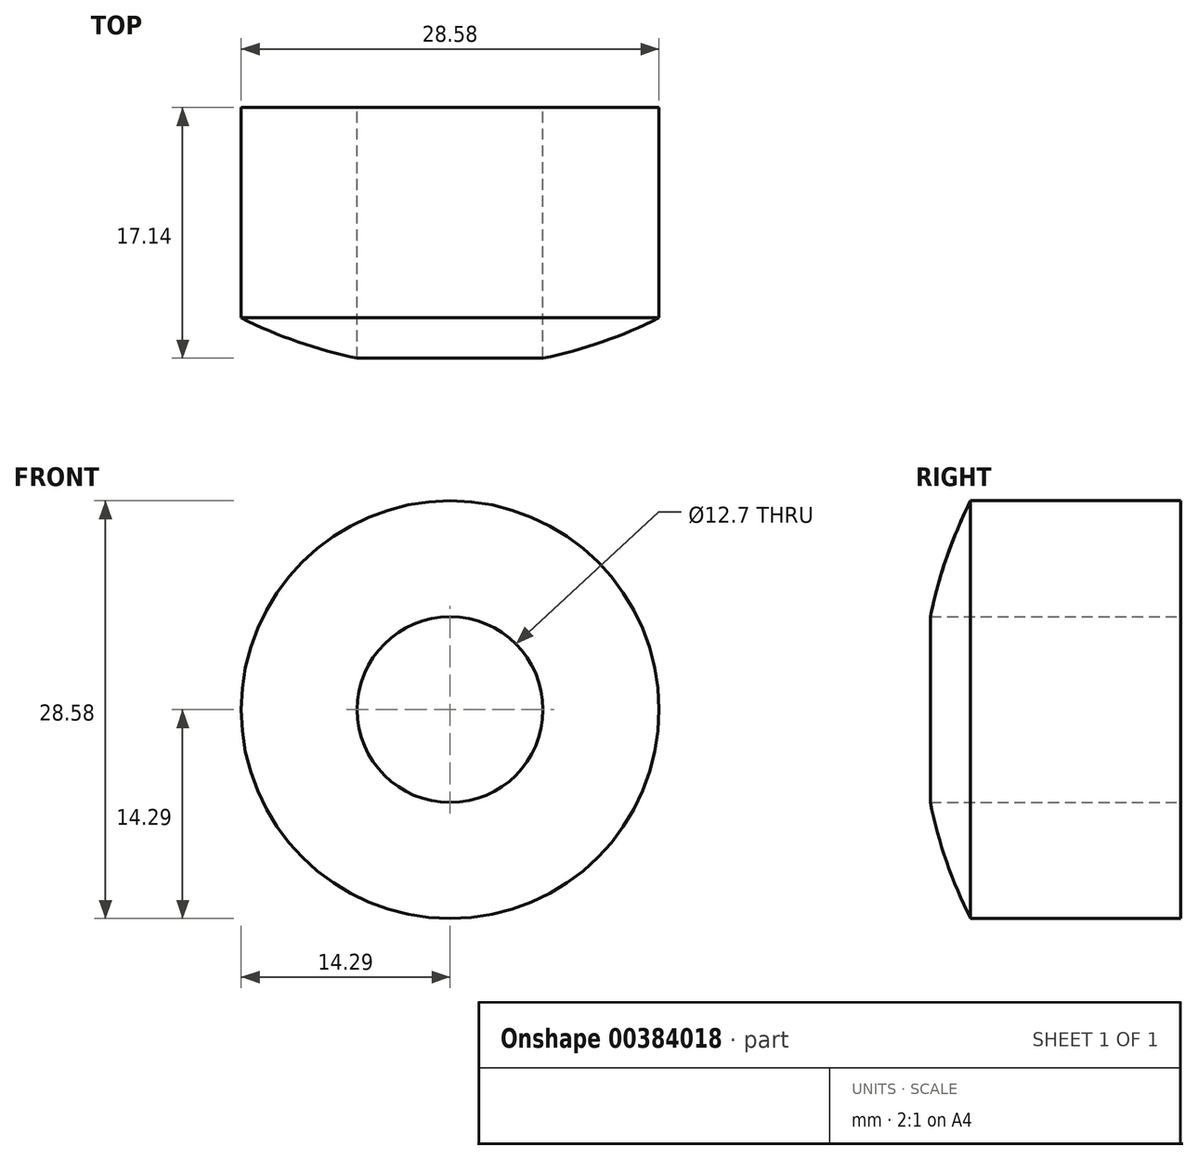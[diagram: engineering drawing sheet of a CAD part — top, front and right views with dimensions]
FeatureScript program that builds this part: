
annotation { "Feature Type Name" : "Feature", "Feature Type Description" : "" }
export const myFeature = defineFeature(function(context is Context, id is Id, definition is map)
    precondition{}
    {
        {
            var Q0;
            Q0=qCreatedBy(makeId("Top.planeOp"),FACE);
            var sketch = newSketch(context, id + "F0", { "sketchPlane" : qUnion([Q0])});
            skCircle(sketch, "E0", {"center": v(0, 0) * mm, "radius": 31.75 * mm});
            skLineSegment(sketch, "E1", {"start": v(0, 31.75) * mm, "end": v(0, -31.75) * mm});
            skSolve(sketch);
        }
        {
            var Q0;
            {var subQ0=sQuery(id+"F0.wireOp",EDGE,"E1");Q0=makeQuery(id+"F0.imprint","IMPRINT",FACE,{"disambiguationData":[TD([[makeQuery(id+"F0.imprint","IMPRINT",EDGE,{"derivedFrom":subQ0}),1.0]])]});}
            var Q1;
            Q1=sQuery(id+"F0.wireOp",EDGE,"E1");
            revolve(context, id + "F1", {"entities" : qUnion([Q0]), "axis" : qUnion([Q1]), "revolveType" : RevolveType.FULL});
        }
        {
            var Q0;
            Q0=qCreatedBy(makeId("Front.planeOp"),FACE);
            var sketch = newSketch(context, id + "F2", { "sketchPlane" : qUnion([Q0])});
            skCircle(sketch, "E2", {"center": v(0, 0) * mm, "radius": 14.29 * mm});
            skCircle(sketch, "E3", {"center": v(0, 0) * mm, "radius": 54.44 * mm});
            skSolve(sketch);
        }
        {
            var Q0;
            Q0 = qSketchRegion(id + "F2", true);
            extrude(context, id + "F3", {"entities" : qUnion([Q0]), "operationType" : NewBodyOperationType.REMOVE, "endBound" : BoundingType.THROUGH_ALL, "depth" : 25.4 * mm, "hasSecondDirection" : true, "secondDirectionBound" : SecondDirectionBoundingType.THROUGH_ALL, "secondDirectionOppositeDirection" : true, "secondDirectionDepth" : 25.4 * mm});
        }
        {
            var Q0;
            Q0=qCreatedBy(makeId("Front.planeOp"),FACE);
            cPlane(context, id + "F4", {"entities" : qUnion([Q0]), "cplaneType" : CPlaneType.OFFSET, "offset" : 13.97 * mm, "width" : 152.4 * mm, "height" : 152.4 * mm});
        }
        {
            var Q0;
            Q0=qCreatedBy(id+"F4.planeOp",FACE);
            var sketch = newSketch(context, id + "F5", { "sketchPlane" : qUnion([Q0])});
            skCircle(sketch, "E4", {"center": v(0, 0) * mm, "radius": 27 * mm});
            skSolve(sketch);
        }
        {
            var Q0;
            Q0 = qSketchRegion(id + "F5", true);
            extrude(context, id + "F6", {"entities" : qUnion([Q0]), "operationType" : NewBodyOperationType.REMOVE, "endBound" : BoundingType.THROUGH_ALL, "oppositeDirection" : true, "depth" : 25.4 * mm});
        }
        {
            var Q0;
            Q0=qCreatedBy(id+"F4.planeOp",FACE);
            var sketch = newSketch(context, id + "F7", { "sketchPlane" : qUnion([Q0])});
            skCircle(sketch, "E5", {"center": v(0, 0) * mm, "radius": 6.35 * mm});
            skSolve(sketch);
        }
        {
            var Q0;
            Q0 = qSketchRegion(id + "F7", true);
            extrude(context, id + "F8", {"entities" : qUnion([Q0]), "operationType" : NewBodyOperationType.REMOVE, "endBound" : BoundingType.THROUGH_ALL, "depth" : 25.4 * mm});
        }
    });
